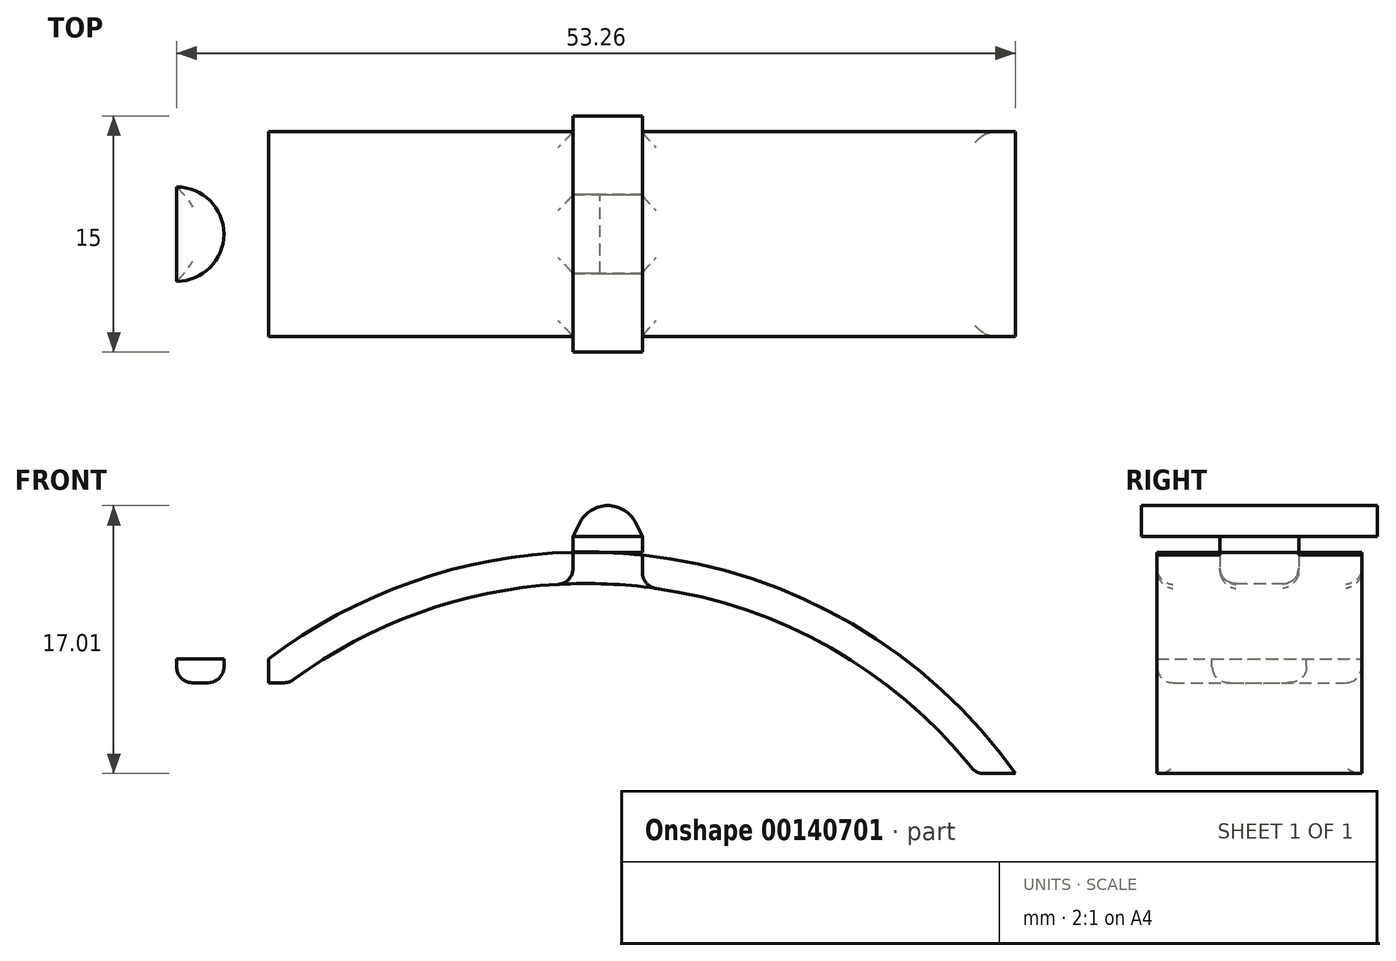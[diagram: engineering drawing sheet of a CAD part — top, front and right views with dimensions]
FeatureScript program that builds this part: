
annotation { "Feature Type Name" : "Feature", "Feature Type Description" : "" }
export const myFeature = defineFeature(function(context is Context, id is Id, definition is map)
    precondition{}
    {
        {
            var Q0;
            Q0=qCreatedBy(makeId("Front.planeOp"),FACE);
            var sketch = newSketch(context, id + "F0", { "sketchPlane" : qUnion([Q0])});
            skArc(sketch, "E0", {"start": v(13.38, -3.25) * mm, "mid": v(-7.25, 8.54) * mm, "end": v(-30.23, 2.52) * mm});
            skArc(sketch, "E1.0", {"start": v(15.87, -3.25) * mm, "mid": v(-7.48, 10.59) * mm, "end": v(-33.4, 2.52) * mm});
            skLineSegment(sketch, "E2", {"start": v(-33.4, 2.52) * mm, "end": v(-30.23, 2.52) * mm});
            skLineSegment(sketch, "E3", {"start": v(15.87, -3.25) * mm, "end": v(13.38, -3.25) * mm});
            skLineSegment(sketch, "E4", {"start": v(-30.23, 2.52) * mm, "end": v(-12.23, 2.52) * mm, "construction": true});
            skLineSegment(sketch, "E5", {"start": v(-12.23, 2.52) * mm, "end": v(-12.23, 12.7) * mm, "construction": true});
            skLineSegment(sketch, "E6", {"start": v(-33.4, 2.52) * mm, "end": v(-37.4, 2.52) * mm});
            skLineSegment(sketch, "E7", {"start": v(-31.56, 4.02) * mm, "end": v(-37.4, 4.02) * mm});
            skLineSegment(sketch, "E8", {"start": v(-37.4, 4.02) * mm, "end": v(-37.4, 2.52) * mm});
            skLineSegment(sketch, "E9.bottom", {"start": v(-12.23, 10.8) * mm, "end": v(-7.81, 10.8) * mm});
            skLineSegment(sketch, "E9.top", {"start": v(-12.23, 11.8) * mm, "end": v(-7.81, 11.8) * mm});
            skLineSegment(sketch, "E9.left", {"start": v(-12.23, 10.8) * mm, "end": v(-12.23, 11.8) * mm});
            skLineSegment(sketch, "E9.right", {"start": v(-7.81, 10.8) * mm, "end": v(-7.81, 11.8) * mm});
            skLineSegment(sketch, "E10", {"start": v(-7.81, 10.8) * mm, "end": v(-7.81, 10.63) * mm});
            skLineSegment(sketch, "E11", {"start": v(-12.23, 11.8) * mm, "end": v(-10.02, 16.3) * mm});
            skLineSegment(sketch, "E12", {"start": v(-10.02, 16.3) * mm, "end": v(-7.81, 11.8) * mm});
            skLineSegment(sketch, "E13", {"start": v(-12.23, 10.8) * mm, "end": v(-12.23, 8.8) * mm});
            skLineSegment(sketch, "E14", {"start": v(-7.81, 10.63) * mm, "end": v(-7.81, 8.61) * mm});
            skSolve(sketch);
        }
        {
            var Q0;
            {var subQ0=sQuery(id+"F0.wireOp",EDGE,"E2");Q0=makeQuery(id+"F0.imprint","IMPRINT",FACE,{"disambiguationData":[TD([[makeQuery(id+"F0.imprint","IMPRINT",EDGE,{"derivedFrom":subQ0}),1.0]])]});}
            var Q1;
            {var subQ0=sQuery(id+"F0.wireOp",EDGE,"E3");Q1=makeQuery(id+"F0.imprint","IMPRINT",FACE,{"disambiguationData":[TD([[makeQuery(id+"F0.imprint","IMPRINT",EDGE,{"derivedFrom":subQ0}),-1.0]])]});}
            var Q2;
            {var subQ0=sQuery(id+"F0.wireOp",EDGE,"E6");Q2=makeQuery(id+"F0.imprint","IMPRINT",FACE,{"disambiguationData":[TD([[makeQuery(id+"F0.imprint","IMPRINT",EDGE,{"derivedFrom":subQ0}),-1.0]])]});}
            extrude(context, id + "F1", {"entities" : qUnion([Q0, Q1, Q2]), "endBound" : BoundingType.SYMMETRIC, "depth" : 13 * mm});
        }
        {
            var Q0;
            {var subQ0=sQuery(id+"F0.wireOp",EDGE,"E13");Q0=makeQuery(id+"F0.imprint","IMPRINT",FACE,{"disambiguationData":[TD([[makeQuery(id+"F0.imprint","IMPRINT",EDGE,{"derivedFrom":subQ0}),1.0]])]});}
            extrude(context, id + "F2", {"entities" : qUnion([Q0]), "endBound" : BoundingType.SYMMETRIC, "depth" : 5 * mm});
        }
        {
            var Q0;
            Q0=makeQuery(id+"F0.imprint","IMPRINT",FACE,{"disambiguationData":[TD([[makeQuery(id+"F0.imprint","IMPRINT",EDGE,{"derivedFrom":sQuery(id+"F0.wireOp",EDGE,"E9.top")}),-1.0]])]});
            extrude(context, id + "F3", {"entities" : qUnion([Q0]), "endBound" : BoundingType.SYMMETRIC, "depth" : 5 * mm});
        }
        {
            var Q0;
            Q0=makeQuery(id+"F0.imprint","IMPRINT",FACE,{"disambiguationData":[TD([[makeQuery(id+"F0.imprint","IMPRINT",EDGE,{"derivedFrom":sQuery(id+"F0.wireOp",EDGE,"E9.top")}),1.0]])]});
            extrude(context, id + "F4", {"entities" : qUnion([Q0]), "operationType" : NewBodyOperationType.ADD, "endBound" : BoundingType.SYMMETRIC, "depth" : 15 * mm});
        }
        {
            var Q0;
            Q0=makeQuery(id+"F1.opExtrude","SWEPT_BODY",BODY,{"disambiguationData":[OSD([sQuery(id+"F0.wireOp",EDGE,"E0"),sQuery(id+"F0.wireOp",EDGE,"E1.0"),sQuery(id+"F0.wireOp",EDGE,"E3"),sQuery(id+"F0.wireOp",EDGE,"E14")])]});
            var Q1;
            Q1=makeQuery(id+"F1.opExtrude","SWEPT_BODY",BODY,{"disambiguationData":[OSD([sQuery(id+"F0.wireOp",EDGE,"E0"),sQuery(id+"F0.wireOp",EDGE,"E1.0"),sQuery(id+"F0.wireOp",EDGE,"E2"),sQuery(id+"F0.wireOp",EDGE,"E6"),sQuery(id+"F0.wireOp",EDGE,"E7"),sQuery(id+"F0.wireOp",EDGE,"E8"),sQuery(id+"F0.wireOp",EDGE,"E13")])]});
            var Q2;
            Q2=makeQuery(id+"F2.opExtrude","SWEPT_BODY",BODY,{"disambiguationData":[OSD([sQuery(id+"F0.wireOp",EDGE,"E0"),sQuery(id+"F0.wireOp",EDGE,"E1.0"),sQuery(id+"F0.wireOp",EDGE,"E9.bottom"),sQuery(id+"F0.wireOp",EDGE,"E13"),sQuery(id+"F0.wireOp",EDGE,"E14")])]});
            var Q3;
            Q3=makeQuery(id+"F3.opExtrude","SWEPT_BODY",BODY,{"disambiguationData":[OSD([sQuery(id+"F0.wireOp",EDGE,"E1.0"),sQuery(id+"F0.wireOp",EDGE,"E9.bottom"),sQuery(id+"F0.wireOp",EDGE,"E9.top"),sQuery(id+"F0.wireOp",EDGE,"E9.left"),sQuery(id+"F0.wireOp",EDGE,"E9.right")])]});
            booleanBodies(context, id + "F5", {"operationType" : BooleanOperationType.UNION, "tools" : qUnion([Q0, Q1, Q2, Q3])});
        }
        {
            var Q0;
            Q0=makeQuery(id+"F1.opExtrude","SWEPT_FACE",FACE,{"disambiguationData":[OSD([sQuery(id+"F0.wireOp",EDGE,"E7")])]});
            var sketch = newSketch(context, id + "F6", { "sketchPlane" : qUnion([Q0])});
            skLineSegment(sketch, "E15.0", {"start": v(-31.56, 6.5) * mm, "end": v(-37.4, 6.5) * mm});
            skLineSegment(sketch, "E15.1", {"start": v(-37.4, -6.5) * mm, "end": v(-37.4, 6.5) * mm});
            skLineSegment(sketch, "E15.2", {"start": v(-31.56, -6.5) * mm, "end": v(-37.4, -6.5) * mm});
            skLineSegment(sketch, "E16", {"start": v(-37.4, 6.5) * mm, "end": v(-37.4, 3) * mm});
            skLineSegment(sketch, "E17", {"start": v(-37.4, -6.5) * mm, "end": v(-37.4, -3) * mm});
            skArc(sketch, "E18", {"start": v(-37.4, -3) * mm, "mid": v(-34.4, 0) * mm, "end": v(-37.4, 3) * mm});
            skSolve(sketch);
        }
        {
            var Q0;
            Q0=makeQuery(id+"F6.imprint","IMPRINT",FACE,{"disambiguationData":[TD([[makeQuery(id+"F6.imprint","IMPRINT",EDGE,{"derivedFrom":sQuery(id+"F6.wireOp",EDGE,"E15.1")}),-1.0]])]});
            extrude(context, id + "F7", {"entities" : qUnion([Q0]), "operationType" : NewBodyOperationType.REMOVE, "oppositeDirection" : true, "depth" : 3 * mm});
        }
        {
            var Q0;
            {var subQ0=sQuery(id+"F0.wireOp",EDGE,"E0");Q0=makeQuery(id+"F5.opBoolean","MERGE",FACE,{"derivedFrom":[makeQuery(id+"F1.opExtrude","SWEPT_FACE",FACE,{"disambiguationData":[OSD([subQ0]),TDD([makeQuery(id+"F0.imprint","IMPRINT",EDGE,{"disambiguationData":[TD([[makeQuery(id+"F0.imprint","INTERSECT",VERTEX,{"derivedFrom":[subQ0,sQuery(id+"F0.wireOp",EDGE,"E3")]}),-1.0]])],"derivedFrom":subQ0})])]}),makeQuery(id+"F1.opExtrude","SWEPT_FACE",FACE,{"disambiguationData":[OSD([subQ0]),TDD([makeQuery(id+"F0.imprint","IMPRINT",EDGE,{"disambiguationData":[TD([[makeQuery(id+"F0.imprint","INTERSECT",VERTEX,{"derivedFrom":[subQ0,sQuery(id+"F0.wireOp",EDGE,"E2")]}),1.0]])],"derivedFrom":subQ0})])]}),makeQuery(id+"F2.opExtrude","SWEPT_FACE",FACE,{"disambiguationData":[OSD([subQ0])]})]});}
            var Q1;
            Q1=makeQuery(id+"F1.opExtrude","CAP_EDGE",EDGE,{"disambiguationData":[OSD([sQuery(id+"F0.wireOp",EDGE,"E2"),sQuery(id+"F0.wireOp",EDGE,"E6")])],"isStart":false});
            var Q2;
            {var subQ0=sQuery(id+"F0.wireOp",EDGE,"E8");var subQ1=sQuery(id+"F0.wireOp",EDGE,"E6");var subQ2=sQuery(id+"F0.wireOp",EDGE,"E2");Q2=makeQuery(id+"F7.boolean.opBoolean","SPLIT",EDGE,{"disambiguationData":[TD([makeQuery(id+"F1.opExtrude","CAP_FACE",FACE,{"disambiguationData":[OSD([sQuery(id+"F0.wireOp",EDGE,"E0"),sQuery(id+"F0.wireOp",EDGE,"E1.0"),subQ2,subQ1,sQuery(id+"F0.wireOp",EDGE,"E7"),subQ0,sQuery(id+"F0.wireOp",EDGE,"E13")])],"isStart":false})])],"derivedFrom":makeQuery(id+"F1.opExtrude","SWEPT_EDGE",EDGE,{"disambiguationData":[OSD([subQ1,subQ0])]})});}
            var Q3;
            Q3=makeQuery(id+"F7.boolean.opBoolean","INTERSECT",EDGE,{"derivedFrom":[makeQuery(id+"F1.opExtrude","SWEPT_FACE",FACE,{"disambiguationData":[OSD([sQuery(id+"F0.wireOp",EDGE,"E2"),sQuery(id+"F0.wireOp",EDGE,"E6")])]}),makeQuery(id+"F7.opExtrude","SWEPT_FACE",FACE,{"disambiguationData":[OSD([sQuery(id+"F6.wireOp",EDGE,"E18")])]})]});
            var Q4;
            {var subQ0=sQuery(id+"F0.wireOp",EDGE,"E8");var subQ1=sQuery(id+"F0.wireOp",EDGE,"E6");var subQ2=sQuery(id+"F0.wireOp",EDGE,"E2");Q4=makeQuery(id+"F7.boolean.opBoolean","SPLIT",EDGE,{"disambiguationData":[TD([makeQuery(id+"F1.opExtrude","CAP_FACE",FACE,{"disambiguationData":[OSD([sQuery(id+"F0.wireOp",EDGE,"E0"),sQuery(id+"F0.wireOp",EDGE,"E1.0"),subQ2,subQ1,sQuery(id+"F0.wireOp",EDGE,"E7"),subQ0,sQuery(id+"F0.wireOp",EDGE,"E13")])],"isStart":true})])],"derivedFrom":makeQuery(id+"F1.opExtrude","SWEPT_EDGE",EDGE,{"disambiguationData":[OSD([subQ1,subQ0])]})});}
            var Q5;
            Q5=makeQuery(id+"F1.opExtrude","CAP_EDGE",EDGE,{"disambiguationData":[OSD([sQuery(id+"F0.wireOp",EDGE,"E2"),sQuery(id+"F0.wireOp",EDGE,"E6")])],"isStart":true});
            fillet(context, id + "F8", {"entities" : qUnion([Q0, Q1, Q2, Q3, Q4, Q5]), "radius" : 1 * mm, "tangentPropagation" : true, "allowEdgeOverflow" : false});
        }
        {
            var Q0;
            Q0=makeQuery(id+"F4.opExtrude","SWEPT_EDGE",EDGE,{"disambiguationData":[OSD([sQuery(id+"F0.wireOp",EDGE,"E11"),sQuery(id+"F0.wireOp",EDGE,"E12")])]});
            fillet(context, id + "F9", {"entities" : qUnion([Q0]), "radius" : 2 * mm, "allowEdgeOverflow" : false});
        }
    });
